# Revit family: Plumbing_Valves_Bermad_710-ES_Solenoid_Controlled_Valve Flanged 2.5in-12in
name_source: partatom
category: Pipe Accessories
units: mm (PartAtom-declared; Revit-internal decimal feet)

## family parameters
Always vertical = Yes
Cut with Voids When Loaded = No
Part Type = Valve - Breaks Into
Round Connector Dimension = Use Diameter
Shared = No
Work Plane-Based = No

## types (7) — shared parameters
700EN = No
700ES = Yes
700Grooved = No
700Threaded = No
Act_Ang = 25.00°
Assembly Code = D2020300
D_Table = 700 Revit Sizes
D_Table_Version = 2
Date of publishing = 03/10/2019
Description = Solenoid Controlled Valve
HC = No
Manufacturer = Bermad
Max Working Water Pressure = 27.6 bar
Max Working Water Temperature = 60 °C
Model = 710
PA = No
PA_8 = No
PB = No
Port_Dim = 40 mm  [stored 0.131234 ft]
Product url = www.bermad.com/product/bc-710-p/
Show Actuator Maintenance Space = No
T_from_port = 220 mm
URL = www.Bermad.com
Valve Seires = 700 ES

## per-type parameters (varying)
- 2.5" - DN65: Act_BD=136 mm; Ax=9 mm  [stored 0.0295276 ft]; Ay=72 mm  [stored 0.23622 ft]; Body_Dim=77 mm  [stored 0.252625 ft]; C_Plus=98 mm; D1=86 mm; D2=125 mm; D3=85 mm  [stored 0.278871 ft]; D4=125 mm; D5=86 mm; D6=38 mm  [stored 0.124672 ft]; Flange_Dim=190 mm; Flange_Thick=27 mm  [stored 0.0885827 ft]; H=242 mm; H1=10 mm  [stored 0.0328084 ft]; H2=19 mm  [stored 0.062336 ft]; H3=12 mm  [stored 0.0393701 ft]; H4=32 mm  [stored 0.104987 ft]; H5=9 mm  [stored 0.0295276 ft]; K Coefficient=7.8; L=290 mm; L_Half=145 mm; Nominal Diameter=65 mm  [stored 0.213255 ft]; Port_Downx=78 mm  [stored 0.255906 ft]; Port_Upx=88 mm; Port_W=59 mm  [stored 0.19357 ft]; Port_W2=118 mm; Port_h=55 mm  [stored 0.180446 ft]; W=190 mm; Weight=0.18 kN; h=98 mm
- 3" - DN80: Act_BD=145 mm; Ax=10 mm  [stored 0.0328084 ft]; Ay=102 mm; Body_Dim=85 mm  [stored 0.278871 ft]; C_Plus=98 mm; D1=86 mm; D2=125 mm; D3=85 mm  [stored 0.278871 ft]; D4=125 mm; D5=86 mm; D6=38 mm  [stored 0.124672 ft]; Flange_Dim=210 mm; Flange_Thick=30 mm  [stored 0.0984252 ft]; H=305 mm; H1=10 mm  [stored 0.0328084 ft]; H2=19 mm  [stored 0.062336 ft]; H3=12 mm  [stored 0.0393701 ft]; H4=32 mm  [stored 0.104987 ft]; H5=9 mm  [stored 0.0295276 ft]; K Coefficient=15.2; L=310 mm; L_Half=155 mm; Nominal Diameter=80 mm  [stored 0.262467 ft]; Port_Downx=80 mm  [stored 0.262467 ft]; Port_Upx=85 mm  [stored 0.278871 ft]; Port_W=60 mm  [stored 0.19685 ft]; Port_W2=120 mm; Port_h=61 mm  [stored 0.200131 ft]; W=210 mm; Weight=0.31 kN; h=109 mm
- 4" - DN100: Act_BD=180 mm; Ax=24 mm  [stored 0.0787402 ft]; Ay=104 mm; Body_Dim=120 mm; C_Plus=144 mm; D1=104 mm; D2=153 mm; D3=110 mm; D4=165 mm; D5=124 mm; D6=42 mm  [stored 0.137795 ft]; Flange_Dim=255 mm; Flange_Thick=35 mm  [stored 0.114829 ft]; H=355 mm; H1=16 mm  [stored 0.0524934 ft]; H2=22 mm  [stored 0.0721785 ft]; H3=22 mm  [stored 0.0721785 ft]; H4=28 mm  [stored 0.0918635 ft]; H5=23 mm  [stored 0.0754593 ft]; K Coefficient=7.7; L=350 mm; L_Half=175 mm; Nominal Diameter=100 mm; Port_Downx=107 mm; Port_Upx=107 mm; Port_W=77 mm  [stored 0.252625 ft]; Port_W2=154 mm; Port_h=69 mm  [stored 0.226378 ft]; W=255 mm; Weight=0.44 kN; h=131 mm
- 6" - DN150: Act_BD=277 mm; Ax=28 mm  [stored 0.0918635 ft]; Ay=134 mm; Body_Dim=172 mm; C_Plus=175 mm; D1=132 mm; D2=199 mm; D3=143 mm; D4=200 mm; D5=143 mm; D6=40 mm  [stored 0.131234 ft]; Flange_Dim=320 mm; Flange_Thick=38 mm  [stored 0.124672 ft]; H=411 mm; H1=19 mm  [stored 0.062336 ft]; H2=21 mm  [stored 0.0688976 ft]; H3=26 mm; H4=31 mm  [stored 0.101706 ft]; H5=27 mm  [stored 0.0885827 ft]; K Coefficient=5.1; L=480 mm; L_Half=240 mm; Nominal Diameter=150 mm; Port_Downx=147 mm; Port_Upx=152 mm; Port_W=102 mm; Port_W2=204 mm; Port_h=95 mm; W=320 mm; Weight=0.76 kN; h=163 mm
- 8" - DN200: Act_BD=342 mm; Ax=35 mm  [stored 0.114829 ft]; Ay=171 mm; Body_Dim=219 mm; C_Plus=314 mm; D1=196 mm; D2=262 mm; D3=237 mm; D4=320 mm; D5=258 mm; D6=80 mm  [stored 0.262467 ft]; Flange_Dim=380 mm; Flange_Thick=43 mm  [stored 0.141076 ft]; H=506 mm; H1=20 mm  [stored 0.0656168 ft]; H2=34 mm; H3=32 mm  [stored 0.104987 ft]; H4=50 mm  [stored 0.164042 ft]; H5=45 mm  [stored 0.147638 ft]; K Coefficient=6.7; L=600 mm; L_Half=300 mm; Nominal Diameter=200 mm; Port_Downx=197 mm; Port_Upx=188 mm; Port_W=129 mm; Port_W2=258 mm; Port_h=119 mm; W=380 mm; Weight=1.23 kN; h=193 mm
- 10" - DN250: Act_BD=422 mm; Ax=44 mm; Ay=212 mm; Body_Dim=234 mm; C_Plus=392 mm; D1=249 mm; D2=325 mm; D3=246 mm; D4=390 mm; D5=329 mm; D6=80 mm  [stored 0.262467 ft]; Flange_Dim=450 mm; Flange_Thick=50 mm  [stored 0.164042 ft]; H=600 mm; H1=20 mm  [stored 0.0656168 ft]; H2=38 mm  [stored 0.124672 ft]; H3=32 mm  [stored 0.104987 ft]; H4=60 mm  [stored 0.19685 ft]; H5=50 mm  [stored 0.164042 ft]; K Coefficient=7.5; L=730 mm; L_Half=365 mm; Nominal Diameter=250 mm; Port_Downx=223 mm; Port_Upx=228 mm; Port_W=163 mm; Port_W2=326 mm; Port_h=144 mm; W=450 mm; Weight=1.94 kN; h=227 mm
- 12" - DN300: Act_BD=530 mm; Ax=66 mm  [stored 0.216535 ft]; Ay=280 mm; Body_Dim=335 mm; C_Plus=507 mm; D1=312 mm; D2=404 mm; D3=352 mm; D4=481 mm; D5=384 mm; D6=120 mm; Flange_Dim=530 mm; Flange_Thick=54 mm; H=721 mm; H1=24 mm  [stored 0.0787402 ft]; H2=47 mm  [stored 0.154199 ft]; H3=47 mm  [stored 0.154199 ft]; H4=75 mm  [stored 0.246063 ft]; H5=43 mm  [stored 0.141076 ft]; K Coefficient=5.5; L=850 mm; L_Half=425 mm; Nominal Diameter=300 mm; Port_Downx=248 mm; Port_Upx=253 mm; Port_W=186 mm; Port_W2=372 mm; Port_h=170 mm; W=540 mm; Weight=3.00 kN; h=265 mm

note: [stored X ft] marks values corroborated as IEEE doubles in the binary element streams (Revit-internal decimal feet)

## geometry (parser evidence)
native form markers: Sweep x3
no freeform markers — native parametric forms only
